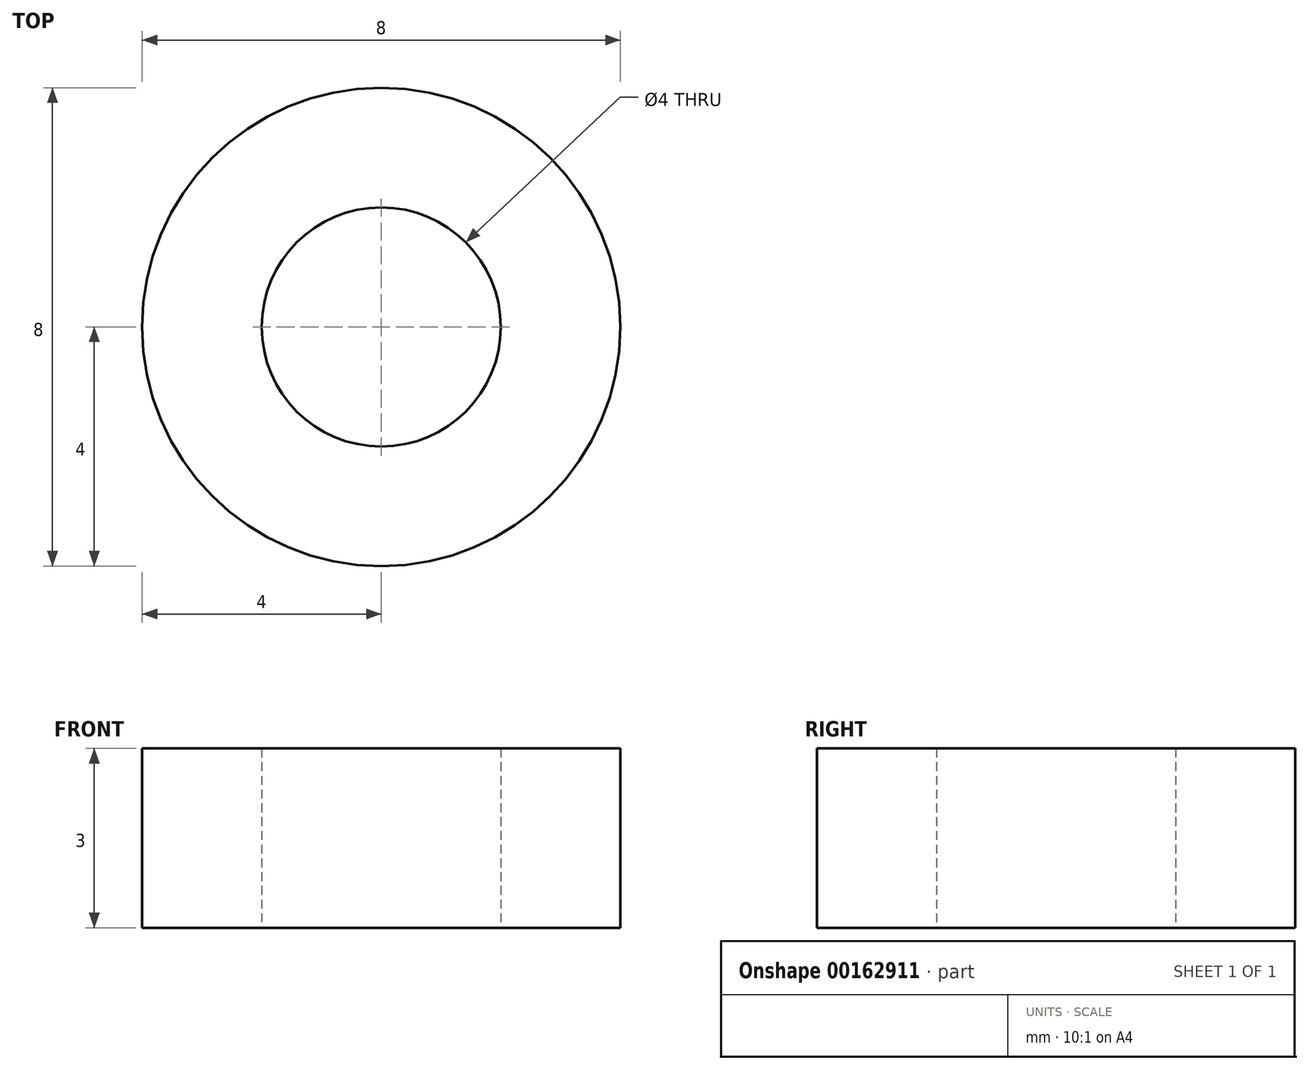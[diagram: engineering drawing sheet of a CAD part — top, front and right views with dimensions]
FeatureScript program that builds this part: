
annotation { "Feature Type Name" : "Feature", "Feature Type Description" : "" }
export const myFeature = defineFeature(function(context is Context, id is Id, definition is map)
    precondition{}
    {
        {
            var Q0;
            Q0=qCreatedBy(makeId("Top.planeOp"),FACE);
            var sketch = newSketch(context, id + "F0", { "sketchPlane" : qUnion([Q0])});
            skCircle(sketch, "E0", {"center": v(0, 0) * mm, "radius": 2 * mm});
            skCircle(sketch, "E1", {"center": v(0, 0) * mm, "radius": 4 * mm});
            skSolve(sketch);
        }
        {
            var Q0;
            Q0=makeQuery(id+"F0.imprint","IMPRINT",FACE,{"disambiguationData":[TD([[makeQuery(id+"F0.imprint","IMPRINT",EDGE,{"derivedFrom":sQuery(id+"F0.wireOp",EDGE,"E0")}),-1.0]])]});
            extrude(context, id + "F1", {"entities" : qUnion([Q0]), "depth" : 3 * mm});
        }
    });
